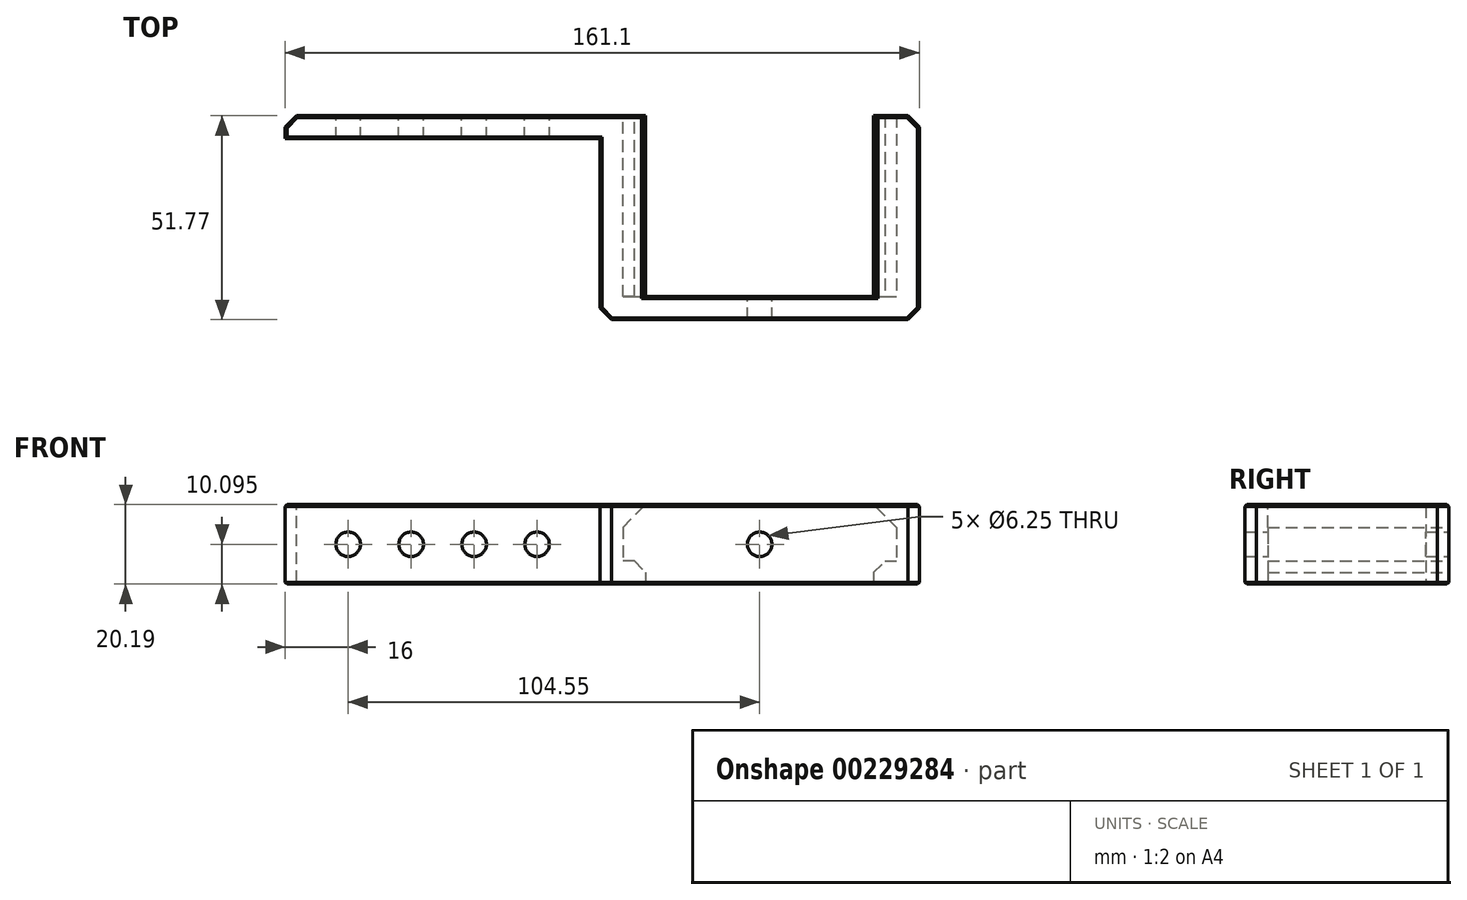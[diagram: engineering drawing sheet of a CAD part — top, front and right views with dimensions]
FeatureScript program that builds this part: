
annotation { "Feature Type Name" : "Feature", "Feature Type Description" : "" }
export const myFeature = defineFeature(function(context is Context, id is Id, definition is map)
    precondition{}
    {
        {
            assignVariable(context, id + "F0", {"name" : "T", "anyValue" : 5.8});
        }
        {
            assignVariable(context, id + "F1", {"name" : "H", "anyValue" : 8.6});
        }
        {
            assignVariable(context, id + "F2", {"name" : "MH", "anyValue" : getVariable(context, 'H') + (getVariable(context, 'T') * 2)});
        }
        {
            var Q0;
            Q0=qCreatedBy(makeId("Top.planeOp"),FACE);
            var sketch = newSketch(context, id + "F3", { "sketchPlane" : qUnion([Q0])});
            skLineSegment(sketch, "E0", {"start": v(0, 0) * mm, "end": v(85.8, 0) * mm});
            skLineSegment(sketch, "E1", {"start": v(85.8, 0) * mm, "end": v(85.8, -45.97) * mm});
            skLineSegment(sketch, "E2", {"start": v(85.8, -45.97) * mm, "end": v(155.3, -45.97) * mm});
            skLineSegment(sketch, "E3", {"start": v(155.3, -45.97) * mm, "end": v(155.3, 0) * mm});
            skLineSegment(sketch, "E4", {"start": v(155.3, 0) * mm, "end": v(161.1, 0) * mm});
            skLineSegment(sketch, "E5", {"start": v(161.1, 0) * mm, "end": v(161.1, -51.77) * mm});
            skLineSegment(sketch, "E6", {"start": v(161.1, -51.77) * mm, "end": v(80, -51.77) * mm});
            skLineSegment(sketch, "E7", {"start": v(80, -51.77) * mm, "end": v(80, -5.8) * mm});
            skLineSegment(sketch, "E8", {"start": v(80, -5.8) * mm, "end": v(0, -5.8) * mm});
            skLineSegment(sketch, "E9", {"start": v(0, -5.8) * mm, "end": v(0, 0) * mm});
            skSolve(sketch);
        }
        {
            var Q0;
            Q0=makeQuery(id+"F3.imprint","IMPRINT",FACE,{"disambiguationData":[TD([[makeQuery(id+"F3.imprint","IMPRINT",EDGE,{"derivedFrom":sQuery(id+"F3.wireOp",EDGE,"E0")}),-1.0]])]});
            extrude(context, id + "F4", {"entities" : qUnion([Q0]), "depth" : (getVariable(context, 'MH')) * mm});
        }
        {
            var Q0;
            Q0=makeQuery(id+"F4.opExtrude","SWEPT_FACE",FACE,{"disambiguationData":[OSD([sQuery(id+"F3.wireOp",EDGE,"E0")])]});
            var sketch = newSketch(context, id + "F5", { "sketchPlane" : qUnion([Q0])});
            skPoint(sketch, "E10", {"position": v(-16, 10.1) * mm});
            skPoint(sketch, "E11", {"position": v(-32, 10.1) * mm});
            skPoint(sketch, "E12", {"position": v(-48, 10.1) * mm});
            skPoint(sketch, "E13", {"position": v(-64, 10.1) * mm});
            skSolve(sketch);
        }
        {
            var Q0;
            Q0=makeQuery(id+"F4.opExtrude","SWEPT_FACE",FACE,{"disambiguationData":[OSD([sQuery(id+"F3.wireOp",EDGE,"E2")])]});
            var sketch = newSketch(context, id + "F6", { "sketchPlane" : qUnion([Q0])});
            skPoint(sketch, "E14", {"position": v(-120.55, 10.1) * mm});
            skPoint(sketch, "E14.positionSnap0", {"position": v(-155.3, 10.1) * mm});
            skSolve(sketch);
        }
        {
            var Q0;
            Q0=sQuery(id+"F5.wireOp",VERTEX,"E10");
            var Q1;
            Q1=sQuery(id+"F5.wireOp",VERTEX,"E11");
            var Q2;
            Q2=sQuery(id+"F5.wireOp",VERTEX,"E12");
            var Q3;
            Q3=sQuery(id+"F5.wireOp",VERTEX,"E13");
            var Q4;
            Q4=sQuery(id+"F6.wireOp",VERTEX,"E14");
            var Q5;
            Q5=makeQuery(id+"F4.opExtrude","SWEPT_BODY",BODY,{"disambiguationData":[OSD([sQuery(id+"F3.wireOp",EDGE,"E0"),sQuery(id+"F3.wireOp",EDGE,"E1"),sQuery(id+"F3.wireOp",EDGE,"E2"),sQuery(id+"F3.wireOp",EDGE,"E3"),sQuery(id+"F3.wireOp",EDGE,"E4"),sQuery(id+"F3.wireOp",EDGE,"E5"),sQuery(id+"F3.wireOp",EDGE,"E6"),sQuery(id+"F3.wireOp",EDGE,"E7"),sQuery(id+"F3.wireOp",EDGE,"E8"),sQuery(id+"F3.wireOp",EDGE,"E9")])]});
            hole(context, id + "F7", {"style" : HoleStyle.SIMPLE, "endStyle" : HoleEndStyle.THROUGH, "standardTappedOrClearance" : lookupTablePath({ "standard" : "ANSI", "size" : "D (0.25)", "type" : "Drilled" }), "standardBlindInLast" : lookupTablePath({ "standard" : "ANSI", "size" : "D", "type" : "Drilled" }), "holeDiameter" : 6.25 * mm, "locations" : qUnion([Q0, Q1, Q2, Q3, Q4]), "scope" : qUnion([Q5]), "isTappedThrough" : true});
        }
        {
            var Q0;
            Q0=makeQuery(id+"F4.opExtrude","SWEPT_FACE",FACE,{"disambiguationData":[OSD([sQuery(id+"F3.wireOp",EDGE,"E3")])]});
            var sketch = newSketch(context, id + "F8", { "sketchPlane" : qUnion([Q0])});
            skLineSegment(sketch, "E15", {"start": v(0, 14.39) * mm, "end": v(45.97, 14.4) * mm});
            skLineSegment(sketch, "E16", {"start": v(0, 5.8) * mm, "end": v(45.97, 5.8) * mm});
            skSolve(sketch);
        }
        {
            var Q0;
            Q0=makeQuery(id+"F4.opExtrude","SWEPT_FACE",FACE,{"disambiguationData":[OSD([sQuery(id+"F3.wireOp",EDGE,"E1")])]});
            var sketch = newSketch(context, id + "F9", { "sketchPlane" : qUnion([Q0])});
            skLineSegment(sketch, "E17", {"start": v(-45.97, 14.39) * mm, "end": v(0, 14.4) * mm});
            skLineSegment(sketch, "E18", {"start": v(-45.97, 5.8) * mm, "end": v(0, 5.8) * mm});
            skSolve(sketch);
        }
        {
            var Q0;
            {var subQ0=sQuery(id+"F8.wireOp",EDGE,"E15");Q0=makeQuery(id+"F8.imprint","IMPRINT",FACE,{"disambiguationData":[TD([[makeQuery(id+"F8.imprint","IMPRINT",EDGE,{"derivedFrom":subQ0}),1.0]])]});}
            var Q1;
            {var subQ0=sQuery(id+"F8.wireOp",EDGE,"E16");Q1=makeQuery(id+"F8.imprint","IMPRINT",FACE,{"disambiguationData":[TD([[makeQuery(id+"F8.imprint","IMPRINT",EDGE,{"derivedFrom":subQ0}),-1.0]])]});}
            extrude(context, id + "F10", {"entities" : qUnion([Q0, Q1]), "operationType" : NewBodyOperationType.ADD, "depth" : (getVariable(context, 'T')) * mm});
        }
        {
            var Q0;
            {var subQ0=sQuery(id+"F9.wireOp",EDGE,"E17");Q0=makeQuery(id+"F9.imprint","IMPRINT",FACE,{"disambiguationData":[TD([[makeQuery(id+"F9.imprint","IMPRINT",EDGE,{"derivedFrom":subQ0}),1.0]])]});}
            var Q1;
            {var subQ0=sQuery(id+"F9.wireOp",EDGE,"E18");Q1=makeQuery(id+"F9.imprint","IMPRINT",FACE,{"disambiguationData":[TD([[makeQuery(id+"F9.imprint","IMPRINT",EDGE,{"derivedFrom":subQ0}),-1.0]])]});}
            extrude(context, id + "F11", {"entities" : qUnion([Q0, Q1]), "operationType" : NewBodyOperationType.ADD, "depth" : (getVariable(context, 'T')) * mm});
        }
        {
            var Q0;
            Q0=makeQuery(id+"F10.opExtrude","CAP_EDGE",EDGE,{"disambiguationData":[OSD([sQuery(id+"F8.wireOp",EDGE,"E15")])],"isStart":false});
            var Q1;
            Q1=makeQuery(id+"F11.opExtrude","CAP_EDGE",EDGE,{"disambiguationData":[OSD([sQuery(id+"F9.wireOp",EDGE,"E17")])],"isStart":false});
            chamfer(context, id + "F12", {"entities" : qUnion([Q0, Q1]), "width" : (getVariable(context, 'T')) * mm, "tangentPropagation" : true});
        }
        {
            var Q0;
            Q0=makeQuery(id+"F4.opExtrude","SWEPT_EDGE",EDGE,{"disambiguationData":[OSD([sQuery(id+"F3.wireOp",EDGE,"E6"),sQuery(id+"F3.wireOp",EDGE,"E7")])]});
            var Q1;
            Q1=makeQuery(id+"F4.opExtrude","SWEPT_EDGE",EDGE,{"disambiguationData":[OSD([sQuery(id+"F3.wireOp",EDGE,"E5"),sQuery(id+"F3.wireOp",EDGE,"E6")])]});
            var Q2;
            Q2=makeQuery(id+"F4.opExtrude","SWEPT_EDGE",EDGE,{"disambiguationData":[OSD([sQuery(id+"F3.wireOp",EDGE,"E0"),sQuery(id+"F3.wireOp",EDGE,"E9")])]});
            var Q3;
            Q3=makeQuery(id+"F4.opExtrude","SWEPT_EDGE",EDGE,{"disambiguationData":[OSD([sQuery(id+"F3.wireOp",EDGE,"E4"),sQuery(id+"F3.wireOp",EDGE,"E5")])]});
            var Q4;
            Q4=makeQuery(id+"F11.opExtrude","CAP_EDGE",EDGE,{"disambiguationData":[OSD([sQuery(id+"F9.wireOp",EDGE,"E18")])],"isStart":false});
            var Q5;
            Q5=makeQuery(id+"F10.opExtrude","CAP_EDGE",EDGE,{"disambiguationData":[OSD([sQuery(id+"F8.wireOp",EDGE,"E16")])],"isStart":false});
            chamfer(context, id + "F13", {"entities" : qUnion([Q0, Q1, Q2, Q3, Q4, Q5]), "width" : (getVariable(context, 'T') / 2) * mm, "tangentPropagation" : true});
        }
        {
            var Q0;
            {var subQ0=sQuery(id+"F3.wireOp",EDGE,"E1");var subQ1=sQuery(id+"F3.wireOp",EDGE,"E3");Q0=makeQuery(id+"F11.boolean.opBoolean","MERGE",FACE,{"derivedFrom":[makeQuery(id+"F10.boolean.opBoolean","MERGE",FACE,{"derivedFrom":[makeQuery(id+"F4.opExtrude","CAP_FACE",FACE,{"disambiguationData":[OSD([sQuery(id+"F3.wireOp",EDGE,"E0"),subQ0,sQuery(id+"F3.wireOp",EDGE,"E2"),subQ1,sQuery(id+"F3.wireOp",EDGE,"E4"),sQuery(id+"F3.wireOp",EDGE,"E5"),sQuery(id+"F3.wireOp",EDGE,"E6"),sQuery(id+"F3.wireOp",EDGE,"E7"),sQuery(id+"F3.wireOp",EDGE,"E8"),sQuery(id+"F3.wireOp",EDGE,"E9")])],"isStart":false}),makeQuery(id+"F10.opExtrude","SWEPT_FACE",FACE,{"disambiguationData":[OSD([subQ1]),TDD([makeQuery(id+"F8.imprint","IMPRINT",EDGE,{"derivedFrom":makeQuery(id+"F4.opExtrude","CAP_EDGE",EDGE,{"disambiguationData":[OSD([subQ1])],"isStart":false})})])]})]}),makeQuery(id+"F11.opExtrude","SWEPT_FACE",FACE,{"disambiguationData":[OSD([subQ0]),TDD([makeQuery(id+"F9.imprint","IMPRINT",EDGE,{"derivedFrom":makeQuery(id+"F4.opExtrude","CAP_EDGE",EDGE,{"disambiguationData":[OSD([subQ0])],"isStart":false})})])]})]});}
            var Q1;
            {var subQ0=sQuery(id+"F3.wireOp",EDGE,"E1");var subQ1=sQuery(id+"F3.wireOp",EDGE,"E3");Q1=makeQuery(id+"F11.boolean.opBoolean","MERGE",FACE,{"derivedFrom":[makeQuery(id+"F10.boolean.opBoolean","MERGE",FACE,{"derivedFrom":[makeQuery(id+"F4.opExtrude","CAP_FACE",FACE,{"disambiguationData":[OSD([sQuery(id+"F3.wireOp",EDGE,"E0"),subQ0,sQuery(id+"F3.wireOp",EDGE,"E2"),subQ1,sQuery(id+"F3.wireOp",EDGE,"E4"),sQuery(id+"F3.wireOp",EDGE,"E5"),sQuery(id+"F3.wireOp",EDGE,"E6"),sQuery(id+"F3.wireOp",EDGE,"E7"),sQuery(id+"F3.wireOp",EDGE,"E8"),sQuery(id+"F3.wireOp",EDGE,"E9")])],"isStart":true}),makeQuery(id+"F10.opExtrude","SWEPT_FACE",FACE,{"disambiguationData":[OSD([subQ1]),TDD([makeQuery(id+"F8.imprint","IMPRINT",EDGE,{"derivedFrom":makeQuery(id+"F4.opExtrude","CAP_EDGE",EDGE,{"disambiguationData":[OSD([subQ1])],"isStart":true})})])]})]}),makeQuery(id+"F11.opExtrude","SWEPT_FACE",FACE,{"disambiguationData":[OSD([subQ0]),TDD([makeQuery(id+"F9.imprint","IMPRINT",EDGE,{"derivedFrom":makeQuery(id+"F4.opExtrude","CAP_EDGE",EDGE,{"disambiguationData":[OSD([subQ0])],"isStart":true})})])]})]});}
            chamfer(context, id + "F14", {"entities" : qUnion([Q0, Q1]), "width" : .45 * mm, "tangentPropagation" : true});
        }
    });
